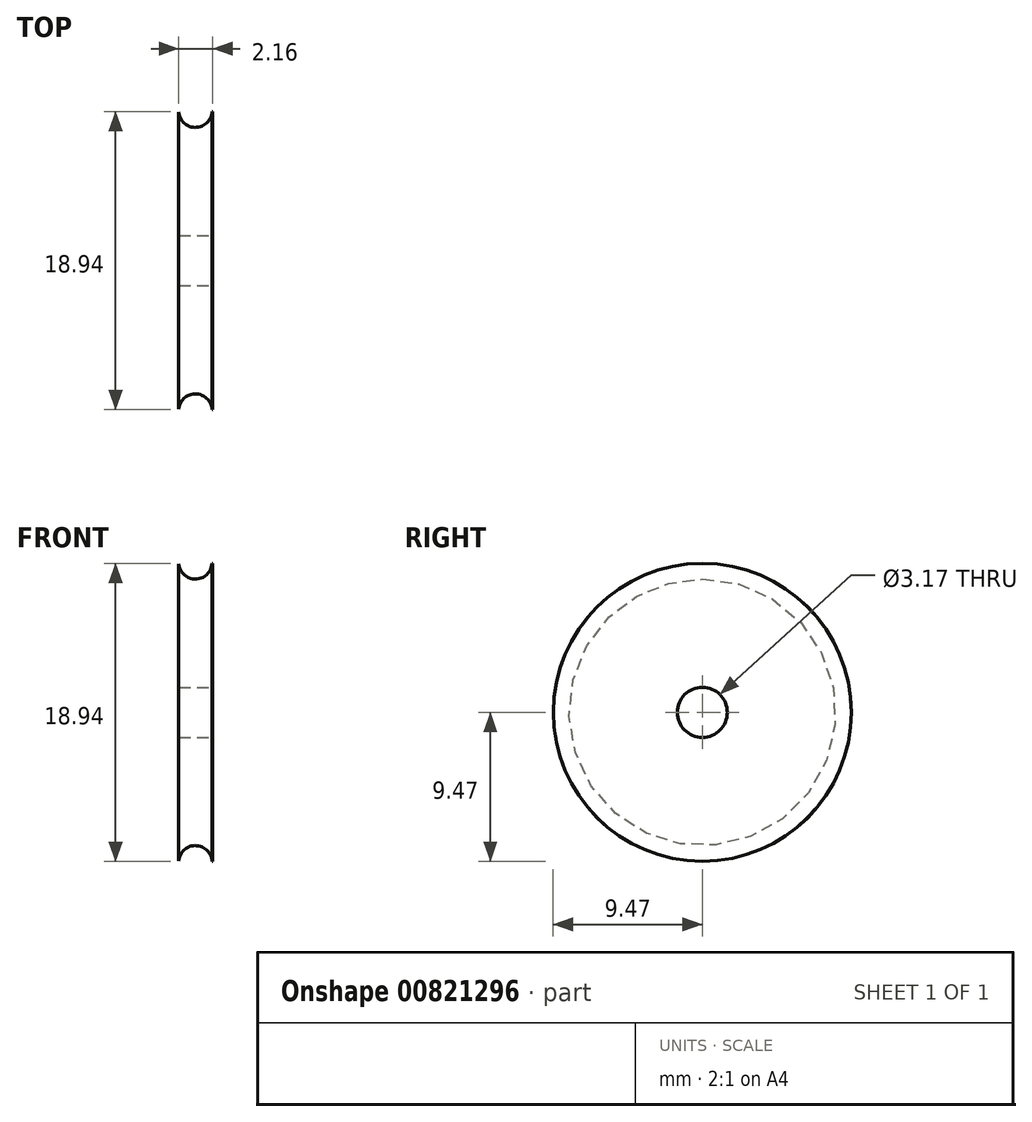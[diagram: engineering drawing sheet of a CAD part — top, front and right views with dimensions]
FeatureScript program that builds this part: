
annotation { "Feature Type Name" : "Feature", "Feature Type Description" : "" }
export const myFeature = defineFeature(function(context is Context, id is Id, definition is map)
    precondition{}
    {
        {
            var Q0;
            Q0=qCreatedBy(makeId("Front.planeOp"),FACE);
            var sketch = newSketch(context, id + "F0", { "sketchPlane" : qUnion([Q0])});
            skCircle(sketch, "E0", {"center": v(0, 0) * mm, "radius": 9.53 * mm});
            skLineSegment(sketch, "E1", {"start": v(-1.06, 0) * mm, "end": v(1.1, 0) * mm});
            skLineSegment(sketch, "E2", {"start": v(-1.06, 0) * mm, "end": v(-1.06, 9.47) * mm});
            skLineSegment(sketch, "E3", {"start": v(1.1, 0) * mm, "end": v(1.1, 9.46) * mm});
            skCircle(sketch, "E4", {"center": v(0, 9.53) * mm, "radius": 1.06 * mm});
            skSolve(sketch);
        }
        {
            var Q0;
            {var subQ1=sQuery(id+"F0.wireOp",EDGE,"E1");Q0=makeQuery(id+"F0.imprint","IMPRINT",FACE,{"disambiguationData":[TD([[makeQuery(id+"F0.imprint","IMPRINT",EDGE,{"derivedFrom":subQ1}),1.0]])]});}
            var Q1;
            Q1=sQuery(id+"F0.wireOp",EDGE,"E1");
            revolve(context, id + "F1", {"surfaceOperationType" : NewSurfaceOperationType.NEW, "entities" : qUnion([Q0]), "axis" : qUnion([Q1]), "revolveType" : RevolveType.FULL});
        }
        {
            var Q0;
            Q0=qCreatedBy(makeId("Right.planeOp"),FACE);
            var sketch = newSketch(context, id + "F2", { "sketchPlane" : qUnion([Q0])});
            skCircle(sketch, "E5", {"center": v(0, 0) * mm, "radius": 1.59 * mm});
            skSolve(sketch);
        }
        {
            var Q0;
            Q0 = qSketchRegion(id + "F2", true);
            extrude(context, id + "F3", {"entities" : qUnion([Q0]), "operationType" : NewBodyOperationType.REMOVE, "oppositeDirection" : true, "depth" : 25.4 * mm, "offsetDistance" : 25.4 * mm, "hasSecondDirection" : true, "secondDirectionOppositeDirection" : false, "secondDirectionDepth" : 25.4 * mm});
        }
    });
